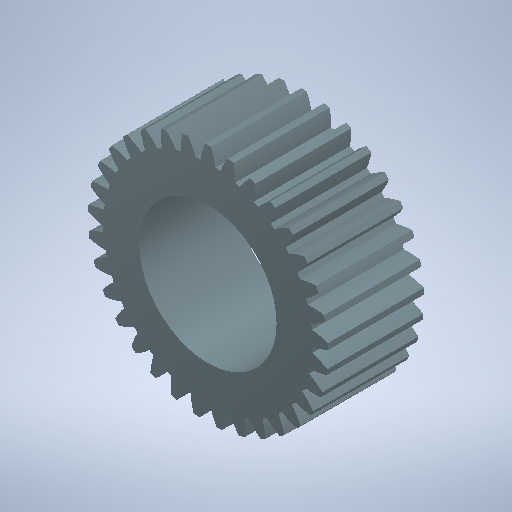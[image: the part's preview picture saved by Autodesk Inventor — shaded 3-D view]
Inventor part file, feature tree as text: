
AUTODESK INVENTOR PART (.ipt)
format: ipt  version: 2025 (Build 290162010, 162A)  size: 411,136 bytes
history: native  units: mm (DEFAULTED — no unit token found)
features: plane x3, other x3, sketch x3, extrude x2
ambient origin geometry x8: Origin, YZ Plane, XZ Plane, XY Plane, X Axis, Y Axis, Z Axis, Center Point
bodies: Body1 (feature_tree), Body2 (feature_tree)
feature tree (11):
  extrude  "Extrusion1"  Depth=7.0mm TaperAngle=0.0deg
  plane  "Work Plane2"
  plane  "Work Plane8"
  plane  "Work Plane9"
  other  "Stirnzahnrad"
  extrude  "Extrusion2"  Depth=10.0mm TaperAngle=0.0deg
  sketch  "Skizze4"  dims[d16=24.75mm d17=0.0mm d34=0.951998mm d39=0.0mm d41=0.0mm d43=24.75mm d46=24.75mm d47=0.0mm d48=0.0mm d49=10.0mm d50=10.0mm d51=0.0mm d52=16.5mm]
  sketch  "Sketch1"  dims[d0=17.5mm d1=7.0mm d2=0.0mm]
  other  "Srf1"
  sketch  "Skizze3"  dims[d3=16.5mm d4=10.0mm d5=0.0mm]
  other  "Flankendurchmesser"
